# Revit family: zzzFaucet-Lavatory-Grohe-Allure_Brilliant-2311500A
name_source: partatom
category: Plumbing Fixtures
units: mm (PartAtom-declared; Revit-internal decimal feet)

## family parameters
Always vertical = No
Cut with Voids When Loaded = No
OmniClass Number = 23.45.55.14
OmniClass Title = Single Faucets
Part Type = Normal
Room Calculation Point = No
Round Connector Dimension = Use Diameter
Shared = Yes
Work Plane-Based = Yes

## types (1)
- 23115000A
    ASME A112.18.1/CSA B125.1 = Yes
    Assembly Code = D2020300
    CW Connection = No
    CWFU = 1.5
    Default Elevation = 0"
    Description = Allure Brilliant Single-Handle Vessel Bathroom Faucet XL-Size
    EPA WaterSense® Certified = Yes
    Energy Policy Act of 1992 = Yes
    Finish = Metal-Grohe-00A-StarLight Chrome
    HW Connection = No
    HWFU = 1.5
    Height = 13 1/8"
    ICC/ANSI A117.1 = Yes
    Installation Instruction Link = https://americanstandard.box.com
    Installation Type = Deck-Mounted
    Length = 6 13/16"
    Manufacturer = Grohe
    Material = Metal-Grohe-00A-StarLight Chrome
    Max. Flow Rate = 1.2 gpm (4.56 L/min)
    Model = 2311500A
    Price = Prices may vary. Please consult Manufacturer Representative for most up-to-date price list.
    Product Documentation Link = https://americanstandard.box.com
    Product Page URL = https://www.grohe.us
    Revised Date = 11/08/2021
    Tempered Water Connection = Yes
    Tempered Water Connection Diameter = 3/8"
    URL = https://www.grohe.us
    US Federal and State material regulations = Yes
    Vent Connection = No
    WFU = 2
    Warranty Documentation Link = https://cdn.cloud.grohe.com
    Waste Connection = Yes
    Width = 3 13/16"

## geometry (parser evidence)
native form markers: Sweep x1
no freeform markers — native parametric forms only
